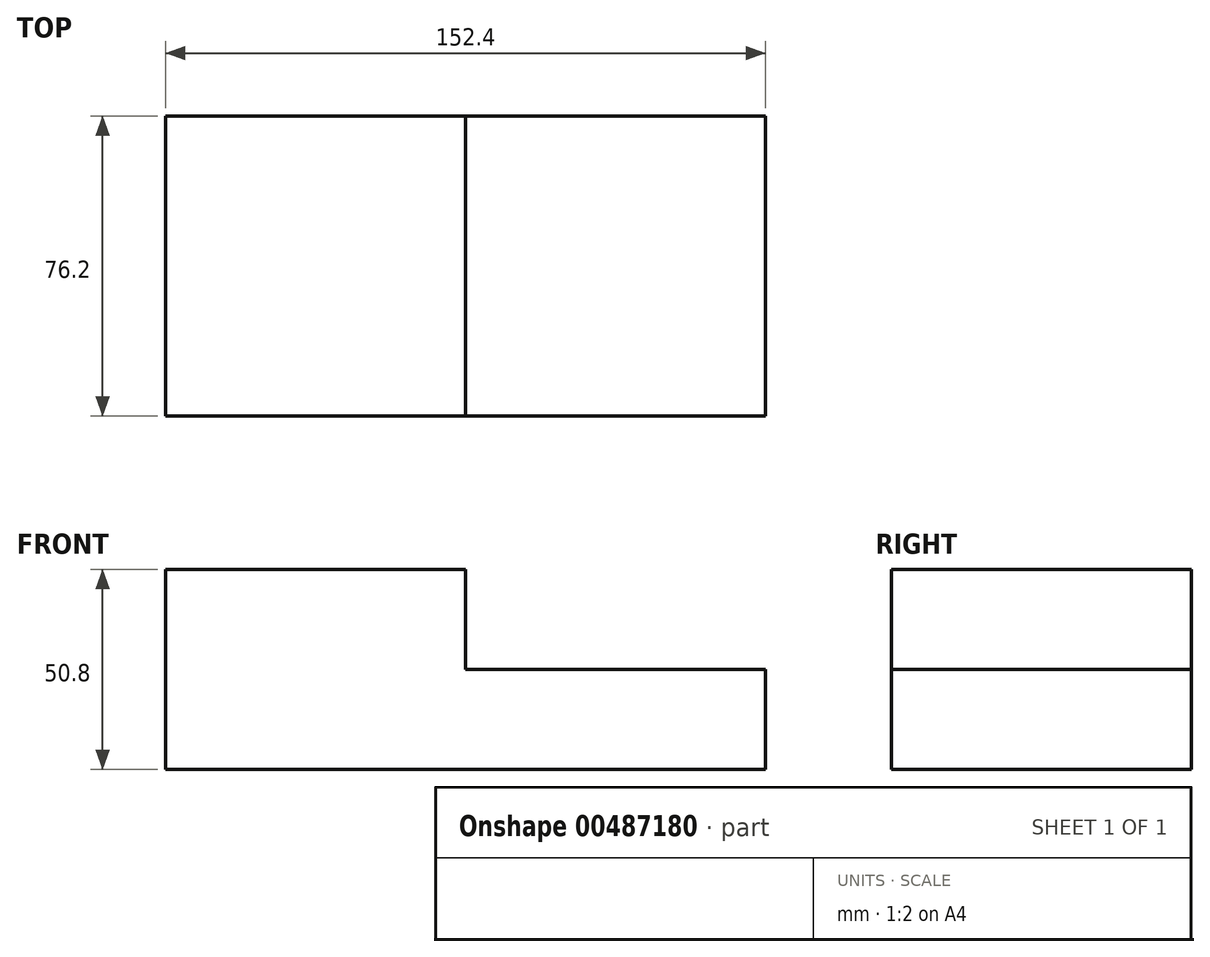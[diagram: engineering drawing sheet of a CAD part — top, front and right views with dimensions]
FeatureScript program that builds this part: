
annotation { "Feature Type Name" : "Feature", "Feature Type Description" : "" }
export const myFeature = defineFeature(function(context is Context, id is Id, definition is map)
    precondition{}
    {
        {
            var Q0;
            Q0=qCreatedBy(makeId("Front.planeOp"),FACE);
            var sketch = newSketch(context, id + "F0", { "sketchPlane" : qUnion([Q0])});
            skLineSegment(sketch, "E0", {"start": v(-108.36, 56.45) * mm, "end": v(-32.16, 56.45) * mm});
            skLineSegment(sketch, "E1", {"start": v(-32.16, 56.45) * mm, "end": v(-32.16, 31.05) * mm});
            skLineSegment(sketch, "E2", {"start": v(-32.16, 31.05) * mm, "end": v(44.04, 31.05) * mm});
            skLineSegment(sketch, "E3", {"start": v(44.04, 31.05) * mm, "end": v(44.04, 5.65) * mm});
            skLineSegment(sketch, "E4", {"start": v(44.04, 5.65) * mm, "end": v(-108.36, 5.65) * mm});
            skLineSegment(sketch, "E5", {"start": v(-108.36, 5.65) * mm, "end": v(-108.36, 56.45) * mm});
            skSolve(sketch);
        }
        {
            var Q0;
            Q0=makeQuery(id+"F0.imprint","IMPRINT",FACE,{"disambiguationData":[TD([[makeQuery(id+"F0.imprint","IMPRINT",EDGE,{"derivedFrom":sQuery(id+"F0.wireOp",EDGE,"E0")}),-1.0]])]});
            extrude(context, id + "F1", {"entities" : qUnion([Q0]), "depth" : 76.2 * mm});
        }
    });
